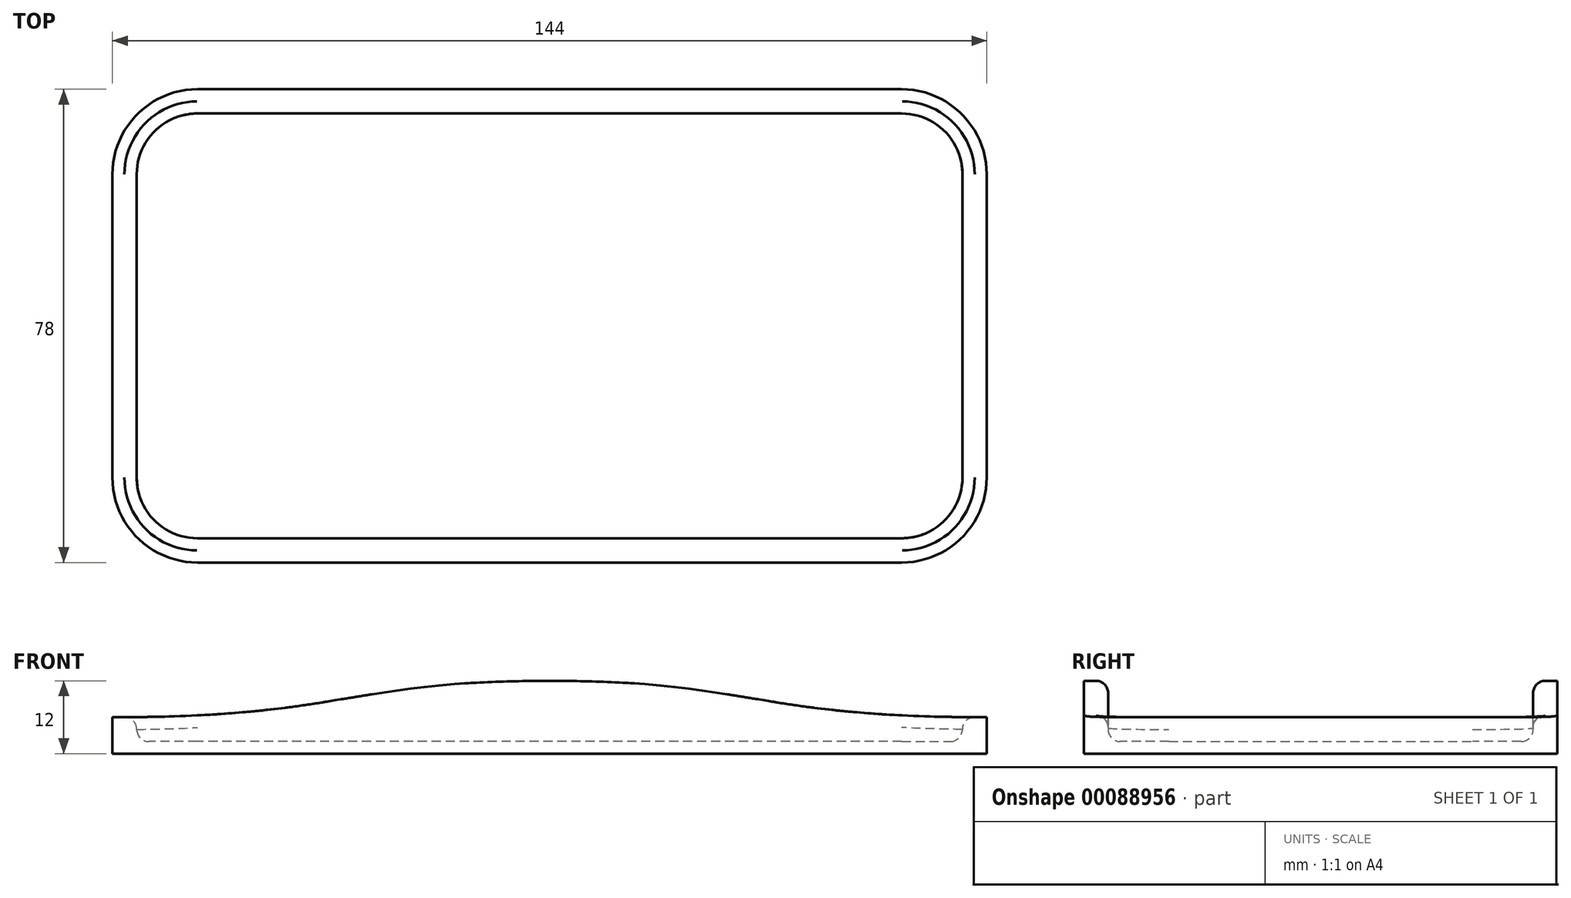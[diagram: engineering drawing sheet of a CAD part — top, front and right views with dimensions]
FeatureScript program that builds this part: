
annotation { "Feature Type Name" : "Feature", "Feature Type Description" : "" }
export const myFeature = defineFeature(function(context is Context, id is Id, definition is map)
    precondition{}
    {
        {
            var Q0;
            Q0=qCreatedBy(makeId("Top.planeOp"),FACE);
            var sketch = newSketch(context, id + "F0", { "sketchPlane" : qUnion([Q0])});
            skLineSegment(sketch, "E0.bottom", {"start": v(58, -35) * mm, "end": v(-58, -35) * mm});
            skLineSegment(sketch, "E0.top", {"start": v(58, 35) * mm, "end": v(-58, 35) * mm});
            skLineSegment(sketch, "E0.left", {"start": v(68, -25) * mm, "end": v(68, 25) * mm});
            skLineSegment(sketch, "E0.right", {"start": v(-68, -25) * mm, "end": v(-68, 25) * mm});
            skPoint(sketch, "E0.middle", {"position": v(0, 0) * mm});
            skPoint(sketch, "E1.visualSharp", {"position": v(-68, 35) * mm});
            skArc(sketch, "E1.filletArc", {"start": v(-58, 35) * mm, "mid": v(-65.07, 32.07) * mm, "end": v(-68, 25) * mm});
            skPoint(sketch, "E2.visualSharp", {"position": v(-68, -35) * mm});
            skArc(sketch, "E2.filletArc", {"start": v(-68, -25) * mm, "mid": v(-65.07, -32.07) * mm, "end": v(-58, -35) * mm});
            skPoint(sketch, "E3.visualSharp", {"position": v(68, -35) * mm});
            skArc(sketch, "E3.filletArc", {"start": v(58, -35) * mm, "mid": v(65.07, -32.07) * mm, "end": v(68, -25) * mm});
            skPoint(sketch, "E4.visualSharp", {"position": v(68, 35) * mm});
            skArc(sketch, "E4.filletArc", {"start": v(68, 25) * mm, "mid": v(65.07, 32.07) * mm, "end": v(58, 35) * mm});
            skArc(sketch, "E5.0", {"start": v(72, 25) * mm, "mid": v(67.9, 34.9) * mm, "end": v(58, 39) * mm});
            skLineSegment(sketch, "E5.1", {"start": v(72, -25) * mm, "end": v(72, 25) * mm});
            skLineSegment(sketch, "E5.2", {"start": v(58, 39) * mm, "end": v(-58, 39) * mm});
            skArc(sketch, "E5.3", {"start": v(58, -39) * mm, "mid": v(67.9, -34.9) * mm, "end": v(72, -25) * mm});
            skArc(sketch, "E5.4", {"start": v(-58, 39) * mm, "mid": v(-67.9, 34.9) * mm, "end": v(-72, 25) * mm});
            skLineSegment(sketch, "E5.5", {"start": v(-72, -25) * mm, "end": v(-72, 25) * mm});
            skArc(sketch, "E5.6", {"start": v(-72, -25) * mm, "mid": v(-67.9, -34.9) * mm, "end": v(-58, -39) * mm});
            skLineSegment(sketch, "E5.7", {"start": v(58, -39) * mm, "end": v(-58, -39) * mm});
            skSolve(sketch);
        }
        {
            var Q0;
            Q0=makeQuery(id+"F0.imprint","IMPRINT",FACE,{"disambiguationData":[TD([[makeQuery(id+"F0.imprint","IMPRINT",EDGE,{"derivedFrom":sQuery(id+"F0.wireOp",EDGE,"E0.bottom")}),-1.0]])]});
            extrude(context, id + "F1", {"entities" : qUnion([Q0]), "depth" : 2 * mm});
        }
        {
            var Q0;
            Q0=makeQuery(id+"F0.imprint","IMPRINT",FACE,{"disambiguationData":[TD([[makeQuery(id+"F0.imprint","IMPRINT",EDGE,{"derivedFrom":sQuery(id+"F0.wireOp",EDGE,"E0.bottom")}),1.0]])]});
            extrude(context, id + "F2", {"entities" : qUnion([Q0]), "operationType" : NewBodyOperationType.ADD, "depth" : 12 * mm});
        }
        {
            var Q0;
            Q0=qCreatedBy(makeId("Front.planeOp"),FACE);
            var sketch = newSketch(context, id + "F3", { "sketchPlane" : qUnion([Q0])});
            skLineSegment(sketch, "E6.0", {"start": v(58, 12) * mm, "end": v(-58, 12) * mm});
            skLineSegment(sketch, "E7.0", {"start": v(72, 0) * mm, "end": v(-72, 0) * mm});
            skLineSegment(sketch, "E8.0", {"start": v(72, 12) * mm, "end": v(72, 0) * mm});
            skLineSegment(sketch, "E9.0", {"start": v(-72, 12) * mm, "end": v(-72, 0) * mm});
            skFitSpline(sketch, "E10", {"points": [v(-72, 6) * mm, v(0, 12) * mm], "startDerivative": vector(115.65, 0) * mm, "endDerivative": vector(99.87, 0) * mm});
            skLineSegment(sketch, "E11", {"start": v(0, 12) * mm, "end": v(0, 0) * mm, "construction": true});
            skFitSpline(sketch, "E12.MirrorCS", {"points": [v(72, 6) * mm, v(0, 12) * mm], "startDerivative": vector(-115.65, 0) * mm, "endDerivative": vector(-99.87, 0) * mm});
            skPoint(sketch, "E13.orphan", {"position": v(-58, 0) * mm});
            skPoint(sketch, "E14.orphan", {"position": v(58, 0) * mm});
            skSolve(sketch);
        }
        {
            var Q0;
            Q0 = qSketchRegion(id + "F3", true);
            extrude(context, id + "F4", {"entities" : qUnion([Q0]), "operationType" : NewBodyOperationType.INTERSECT, "endBound" : BoundingType.SYMMETRIC, "depth" : 99 * mm});
        }
        {
            var Q0;
            Q0=makeQuery(id+"F2.opExtrude","SWEPT_FACE",FACE,{"disambiguationData":[OSD([sQuery(id+"F0.wireOp",EDGE,"E2.filletArc")])]});
            var Q1;
            Q1=makeQuery(id+"F4.boolean.opBoolean","INTERSECT",EDGE,{"derivedFrom":[makeQuery(id+"F2.opExtrude","SWEPT_FACE",FACE,{"disambiguationData":[OSD([sQuery(id+"F0.wireOp",EDGE,"E5.6")])]}),makeQuery(id+"F4.boolean.toolComplement.opBoolean","COPY",FACE,{"derivedFrom":makeQuery(id+"F4.opExtrude","SWEPT_FACE",FACE,{"disambiguationData":[OSD([sQuery(id+"F3.wireOp",EDGE,"E10")])]})})]});
            fillet(context, id + "F5", {"entities" : qUnion([Q0, Q1]), "radius" : 2 * mm, "tangentPropagation" : true, "allowEdgeOverflow" : false});
        }
    });
